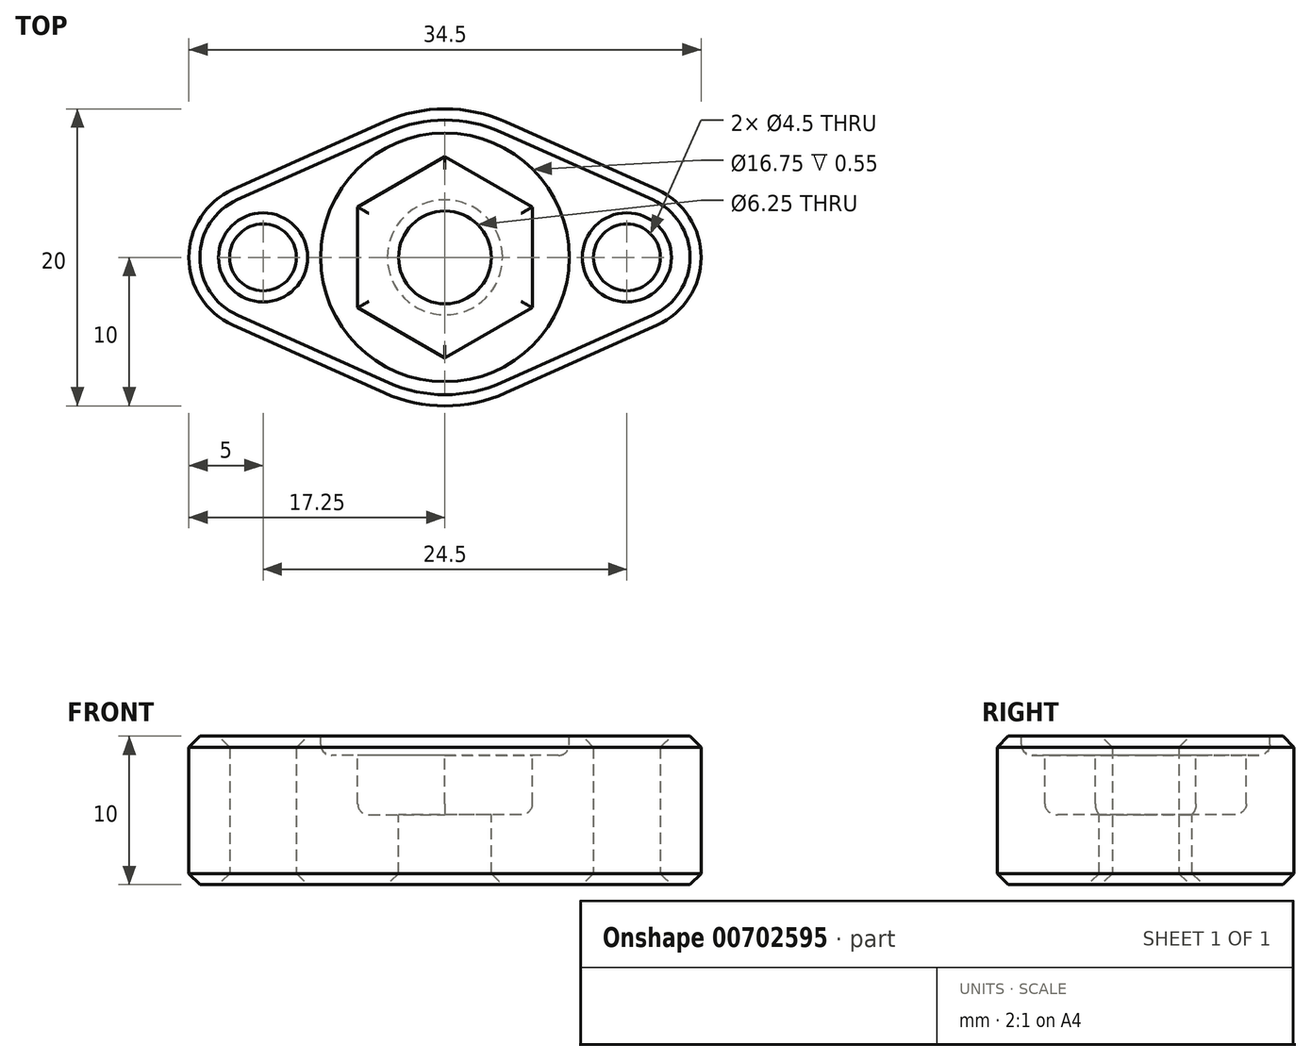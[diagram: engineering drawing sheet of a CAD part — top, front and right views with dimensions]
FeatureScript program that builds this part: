
annotation { "Feature Type Name" : "Feature", "Feature Type Description" : "" }
export const myFeature = defineFeature(function(context is Context, id is Id, definition is map)
    precondition{}
    {
        {
            var Q0;
            Q0=qCreatedBy(makeId("Top.planeOp"),FACE);
            var sketch = newSketch(context, id + "F0", { "sketchPlane" : qUnion([Q0])});
            skArc(sketch, "E0", {"start": v(4.08, 9.13) * mm, "mid": v(0, 10) * mm, "end": v(-4.08, 9.13) * mm});
            skCircle(sketch, "E1", {"center": v(12.25, 0) * mm, "radius": 2.25 * mm});
            skArc(sketch, "E2", {"start": v(14.3, -4.56) * mm, "mid": v(17.25, 0) * mm, "end": v(14.3, 4.56) * mm});
            skLineSegment(sketch, "E3", {"start": v(4.08, 9.13) * mm, "end": v(14.3, 4.56) * mm});
            skLineSegment(sketch, "E4", {"start": v(4.08, -9.13) * mm, "end": v(14.3, -4.56) * mm});
            skCircle(sketch, "E5", {"center": v(-12.25, 0) * mm, "radius": 2.25 * mm});
            skArc(sketch, "E6", {"start": v(-14.3, 4.56) * mm, "mid": v(-17.25, 0) * mm, "end": v(-14.3, -4.56) * mm});
            skLineSegment(sketch, "E7", {"start": v(-14.3, 4.56) * mm, "end": v(-4.08, 9.13) * mm});
            skLineSegment(sketch, "E8", {"start": v(-14.3, -4.56) * mm, "end": v(-4.08, -9.13) * mm});
            skArc(sketch, "E9.trimOffspring", {"start": v(-4.08, -9.13) * mm, "mid": v(0, -10) * mm, "end": v(4.08, -9.13) * mm});
            skSolve(sketch);
        }
        {
            var Q0;
            Q0=makeQuery(id+"F0.imprint","IMPRINT",FACE,{"disambiguationData":[TD([[makeQuery(id+"F0.imprint","IMPRINT",EDGE,{"derivedFrom":sQuery(id+"F0.wireOp",EDGE,"E0")}),1.0]])]});
            extrude(context, id + "F1", {"entities" : qUnion([Q0]), "depth" : 10 * mm, "offsetDistance" : 25 * mm});
        }
        {
            var Q0;
            Q0=makeQuery(id+"F1.opExtrude","CAP_FACE",FACE,{"disambiguationData":[OSD([sQuery(id+"F0.wireOp",EDGE,"E0"),sQuery(id+"F0.wireOp",EDGE,"E1"),sQuery(id+"F0.wireOp",EDGE,"E2"),sQuery(id+"F0.wireOp",EDGE,"E3"),sQuery(id+"F0.wireOp",EDGE,"E4")])],"isStart":false});
            var sketch = newSketch(context, id + "F2", { "sketchPlane" : qUnion([Q0])});
            skCircle(sketch, "E10", {"center": v(0, 0) * mm, "radius": 8.38 * mm});
            skSolve(sketch);
        }
        {
            var Q0;
            Q0=makeQuery(id+"F2.imprint","IMPRINT",FACE,{"disambiguationData":[TD([[makeQuery(id+"F2.imprint","IMPRINT",EDGE,{"derivedFrom":sQuery(id+"F2.wireOp",EDGE,"E10")}),1.0]])]});
            extrude(context, id + "F3", {"entities" : qUnion([Q0]), "operationType" : NewBodyOperationType.REMOVE, "oppositeDirection" : true, "depth" : 1.3 * mm, "offsetDistance" : 25 * mm});
        }
        {
            var Q0;
            Q0=makeQuery(id+"F3.boolean.opBoolean","COPY",FACE,{"derivedFrom":makeQuery(id+"F3.opExtrude","CAP_FACE",FACE,{"disambiguationData":[OSD([sQuery(id+"F2.wireOp",EDGE,"E10")])],"isStart":false})});
            var sketch = newSketch(context, id + "F4", { "sketchPlane" : qUnion([Q0])});
            skCircle(sketch, "E11.cCircle", {"center": v(0, 0) * mm, "radius": 5.88 * mm, "construction": true});
            skLineSegment(sketch, "E11.0", {"start": v(5.88, 3.4) * mm, "end": v(5.88, -3.4) * mm});
            skLineSegment(sketch, "E11.1", {"start": v(5.88, -3.4) * mm, "end": v(0, -6.78) * mm});
            skLineSegment(sketch, "E11.2", {"start": v(0, -6.78) * mm, "end": v(-5.88, -3.4) * mm});
            skLineSegment(sketch, "E11.3", {"start": v(-5.88, -3.4) * mm, "end": v(-5.88, 3.4) * mm});
            skLineSegment(sketch, "E11.4", {"start": v(-5.88, 3.4) * mm, "end": v(0, 6.78) * mm});
            skLineSegment(sketch, "E11.5", {"start": v(0, 6.78) * mm, "end": v(5.88, 3.4) * mm});
            skPoint(sketch, "E11.0.midPoint", {"position": v(5.88, 0) * mm});
            skSolve(sketch);
        }
        {
            var Q0;
            Q0=makeQuery(id+"F4.imprint","IMPRINT",FACE,{"disambiguationData":[TD([[makeQuery(id+"F4.imprint","IMPRINT",EDGE,{"derivedFrom":sQuery(id+"F4.wireOp",EDGE,"E11.0")}),-1.0]])]});
            extrude(context, id + "F5", {"entities" : qUnion([Q0]), "operationType" : NewBodyOperationType.REMOVE, "oppositeDirection" : true, "depth" : 4 * mm, "offsetDistance" : 25 * mm});
        }
        {
            var Q0;
            Q0=makeQuery(id+"F5.boolean.opBoolean","COPY",FACE,{"derivedFrom":makeQuery(id+"F5.opExtrude","CAP_FACE",FACE,{"disambiguationData":[OSD([sQuery(id+"F4.wireOp",EDGE,"E11.0"),sQuery(id+"F4.wireOp",EDGE,"E11.1"),sQuery(id+"F4.wireOp",EDGE,"E11.2"),sQuery(id+"F4.wireOp",EDGE,"E11.3"),sQuery(id+"F4.wireOp",EDGE,"E11.4"),sQuery(id+"F4.wireOp",EDGE,"E11.5")])],"isStart":false})});
            var sketch = newSketch(context, id + "F6", { "sketchPlane" : qUnion([Q0])});
            skCircle(sketch, "E12", {"center": v(0, 0) * mm, "radius": 3.12 * mm});
            skSolve(sketch);
        }
        {
            var Q0;
            Q0=makeQuery(id+"F6.imprint","IMPRINT",FACE,{"disambiguationData":[TD([[makeQuery(id+"F6.imprint","IMPRINT",EDGE,{"derivedFrom":sQuery(id+"F6.wireOp",EDGE,"E12")}),1.0]])]});
            extrude(context, id + "F7", {"entities" : qUnion([Q0]), "operationType" : NewBodyOperationType.REMOVE, "endBound" : BoundingType.THROUGH_ALL, "oppositeDirection" : true, "depth" : 25 * mm, "offsetDistance" : 25 * mm});
        }
        {
            var Q0;
            Q0=makeQuery(id+"F3.boolean.opBoolean","COPY",EDGE,{"derivedFrom":makeQuery(id+"F3.opExtrude","CAP_EDGE",EDGE,{"disambiguationData":[OSD([sQuery(id+"F2.wireOp",EDGE,"E10")])],"isStart":false})});
            var Q1;
            Q1=makeQuery(id+"F5.boolean.opBoolean","COPY",EDGE,{"derivedFrom":makeQuery(id+"F5.opExtrude","CAP_EDGE",EDGE,{"disambiguationData":[OSD([sQuery(id+"F4.wireOp",EDGE,"E11.4")])],"isStart":false})});
            var Q2;
            Q2=makeQuery(id+"F5.boolean.opBoolean","COPY",EDGE,{"derivedFrom":makeQuery(id+"F5.opExtrude","CAP_EDGE",EDGE,{"disambiguationData":[OSD([sQuery(id+"F4.wireOp",EDGE,"E11.5")])],"isStart":false})});
            var Q3;
            Q3=makeQuery(id+"F5.boolean.opBoolean","COPY",EDGE,{"derivedFrom":makeQuery(id+"F5.opExtrude","CAP_EDGE",EDGE,{"disambiguationData":[OSD([sQuery(id+"F4.wireOp",EDGE,"E11.3")])],"isStart":false})});
            var Q4;
            Q4=makeQuery(id+"F5.boolean.opBoolean","COPY",EDGE,{"derivedFrom":makeQuery(id+"F5.opExtrude","CAP_EDGE",EDGE,{"disambiguationData":[OSD([sQuery(id+"F4.wireOp",EDGE,"E11.2")])],"isStart":false})});
            var Q5;
            Q5=makeQuery(id+"F5.boolean.opBoolean","COPY",EDGE,{"derivedFrom":makeQuery(id+"F5.opExtrude","CAP_EDGE",EDGE,{"disambiguationData":[OSD([sQuery(id+"F4.wireOp",EDGE,"E11.1")])],"isStart":false})});
            var Q6;
            Q6=makeQuery(id+"F5.boolean.opBoolean","COPY",EDGE,{"derivedFrom":makeQuery(id+"F5.opExtrude","CAP_EDGE",EDGE,{"disambiguationData":[OSD([sQuery(id+"F4.wireOp",EDGE,"E11.0")])],"isStart":false})});
            fillet(context, id + "F8", {"entities" : qUnion([Q0, Q1, Q2, Q3, Q4, Q5, Q6]), "radius" : 0.75 * mm, "tangentPropagation" : true, "defaultsChanged" : true, "vertexSettings" : [], "allowEdgeOverflow" : false});
        }
        {
            var Q0;
            Q0=makeQuery(id+"F3.boolean.opBoolean","COPY",EDGE,{"derivedFrom":makeQuery(id+"F3.opExtrude","CAP_EDGE",EDGE,{"disambiguationData":[OSD([sQuery(id+"F2.wireOp",EDGE,"E10")])],"isStart":true})});
            var Q1;
            Q1=makeQuery(id+"F1.opExtrude","CAP_EDGE",EDGE,{"disambiguationData":[OSD([sQuery(id+"F0.wireOp",EDGE,"E1")])],"isStart":false});
            var Q2;
            Q2=makeQuery(id+"F1.opExtrude","CAP_EDGE",EDGE,{"disambiguationData":[OSD([sQuery(id+"F0.wireOp",EDGE,"E0")])],"isStart":false});
            var Q3;
            Q3=makeQuery(id+"F1.opExtrude","CAP_EDGE",EDGE,{"disambiguationData":[OSD([sQuery(id+"F0.wireOp",EDGE,"E4")])],"isStart":false});
            var Q4;
            Q4=makeQuery(id+"F1.opExtrude","CAP_EDGE",EDGE,{"disambiguationData":[OSD([sQuery(id+"F0.wireOp",EDGE,"E0")])],"isStart":true});
            var Q5;
            Q5=makeQuery(id+"F1.opExtrude","CAP_EDGE",EDGE,{"disambiguationData":[OSD([sQuery(id+"F0.wireOp",EDGE,"E3")])],"isStart":true});
            var Q6;
            Q6=makeQuery(id+"F7.boolean.opBoolean","INTERSECT",EDGE,{"derivedFrom":[makeQuery(id+"F1.opExtrude","CAP_FACE",FACE,{"disambiguationData":[OSD([sQuery(id+"F0.wireOp",EDGE,"E0"),sQuery(id+"F0.wireOp",EDGE,"E1"),sQuery(id+"F0.wireOp",EDGE,"E2"),sQuery(id+"F0.wireOp",EDGE,"E3"),sQuery(id+"F0.wireOp",EDGE,"E4")])],"isStart":true}),makeQuery(id+"F7.opExtrude","SWEPT_FACE",FACE,{"disambiguationData":[OSD([sQuery(id+"F6.wireOp",EDGE,"E12")])]})]});
            var Q7;
            Q7=makeQuery(id+"F1.opExtrude","CAP_EDGE",EDGE,{"disambiguationData":[OSD([sQuery(id+"F0.wireOp",EDGE,"E1")])],"isStart":true});
            var Q8;
            Q8=makeQuery(id+"F7.boolean.opBoolean","COPY",EDGE,{"derivedFrom":makeQuery(id+"F7.opExtrude","CAP_EDGE",EDGE,{"disambiguationData":[OSD([sQuery(id+"F6.wireOp",EDGE,"E12")])],"isStart":true})});
            var Q9;
            Q9=makeQuery(id+"F1.opExtrude","CAP_EDGE",EDGE,{"disambiguationData":[OSD([sQuery(id+"F0.wireOp",EDGE,"E5")])],"isStart":false});
            var Q10;
            Q10=makeQuery(id+"F1.opExtrude","CAP_EDGE",EDGE,{"disambiguationData":[OSD([sQuery(id+"F0.wireOp",EDGE,"E5")])],"isStart":true});
            chamfer(context, id + "F9", {"entities" : qUnion([Q0, Q1, Q2, Q3, Q4, Q5, Q6, Q7, Q8, Q9, Q10]), "width" : 0.75 * mm, "tangentPropagation" : true});
        }
    });
